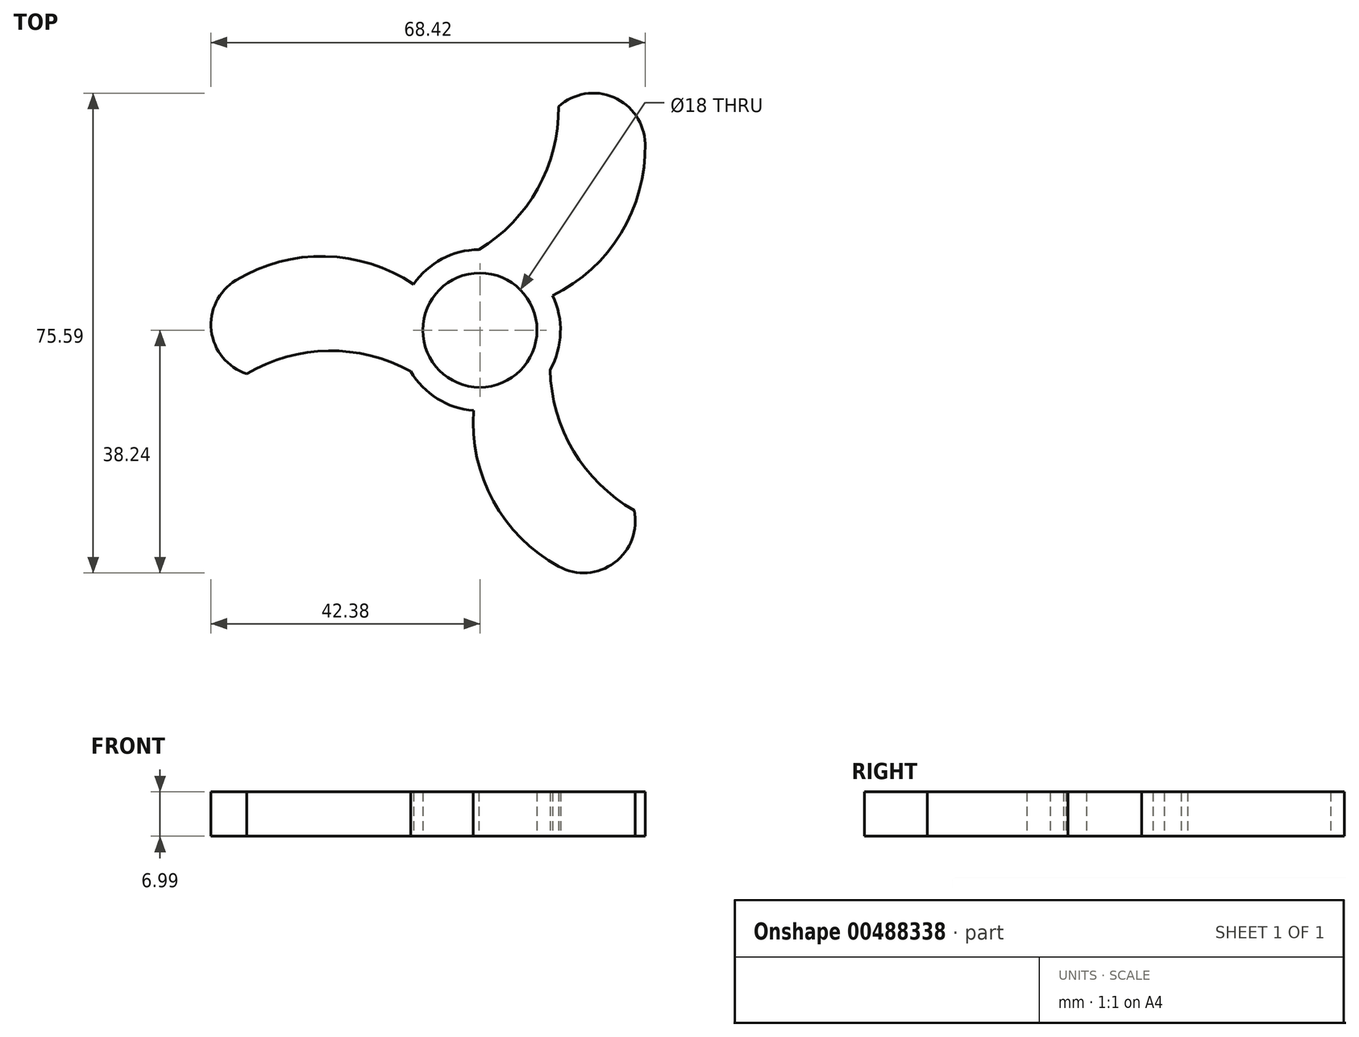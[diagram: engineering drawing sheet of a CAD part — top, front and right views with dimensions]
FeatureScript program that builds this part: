
annotation { "Feature Type Name" : "Feature", "Feature Type Description" : "" }
export const myFeature = defineFeature(function(context is Context, id is Id, definition is map)
    precondition{}
    {
        {
            var Q0;
            Q0=qCreatedBy(makeId("Top.planeOp"),FACE);
            var sketch = newSketch(context, id + "F0", { "sketchPlane" : qUnion([Q0])});
            skCircle(sketch, "E0", {"center": v(0, 0) * mm, "radius": 9 * mm});
            skArc(sketch, "E1", {"start": v(-10.91, -6.5) * mm, "mid": v(-6.71, -10.78) * mm, "end": v(-1.02, -12.66) * mm});
            skArc(sketch, "E2", {"start": v(-10.46, 7.2) * mm, "mid": v(-24.37, 11.63) * mm, "end": v(-38.46, 7.85) * mm});
            skArc(sketch, "E3", {"start": v(-10.91, -6.5) * mm, "mid": v(-23.87, -3.25) * mm, "end": v(-36.73, -6.87) * mm});
            skArc(sketch, "E4", {"start": v(-38.46, 7.85) * mm, "mid": v(-42.32, -0.07) * mm, "end": v(-36.73, -6.87) * mm});
            skArc(sketch, "E5.1.0", {"start": v(-1.02, -12.66) * mm, "mid": v(2.1, -26.92) * mm, "end": v(12.43, -37.24) * mm});
            skArc(sketch, "E5.1.1", {"start": v(11.08, -6.2) * mm, "mid": v(14.75, -19.05) * mm, "end": v(24.32, -28.37) * mm});
            skArc(sketch, "E5.1.2", {"start": v(12.43, -37.24) * mm, "mid": v(21.22, -36.62) * mm, "end": v(24.32, -28.37) * mm});
            skArc(sketch, "E5.2.0", {"start": v(11.47, 5.45) * mm, "mid": v(22.26, 15.29) * mm, "end": v(26.03, 29.38) * mm});
            skArc(sketch, "E5.2.1", {"start": v(-0.17, 12.7) * mm, "mid": v(9.12, 22.3) * mm, "end": v(12.41, 35.24) * mm});
            skArc(sketch, "E5.2.2", {"start": v(26.03, 29.38) * mm, "mid": v(21.1, 36.69) * mm, "end": v(12.41, 35.24) * mm});
            skArc(sketch, "E6.trimOffspring", {"start": v(-0.17, 12.7) * mm, "mid": v(-5.98, 11.2) * mm, "end": v(-10.46, 7.2) * mm});
            skArc(sketch, "E7.trimOffspring", {"start": v(11.08, -6.2) * mm, "mid": v(12.7, -0.43) * mm, "end": v(11.47, 5.45) * mm});
            skSolve(sketch);
        }
        {
            var Q0;
            Q0=makeQuery(id+"F0.imprint","IMPRINT",FACE,{"disambiguationData":[TD([[makeQuery(id+"F0.imprint","IMPRINT",EDGE,{"derivedFrom":sQuery(id+"F0.wireOp",EDGE,"E0")}),-1.0]])]});
            extrude(context, id + "F1", {"entities" : qUnion([Q0]), "depth" : 7 * mm});
        }
    });
